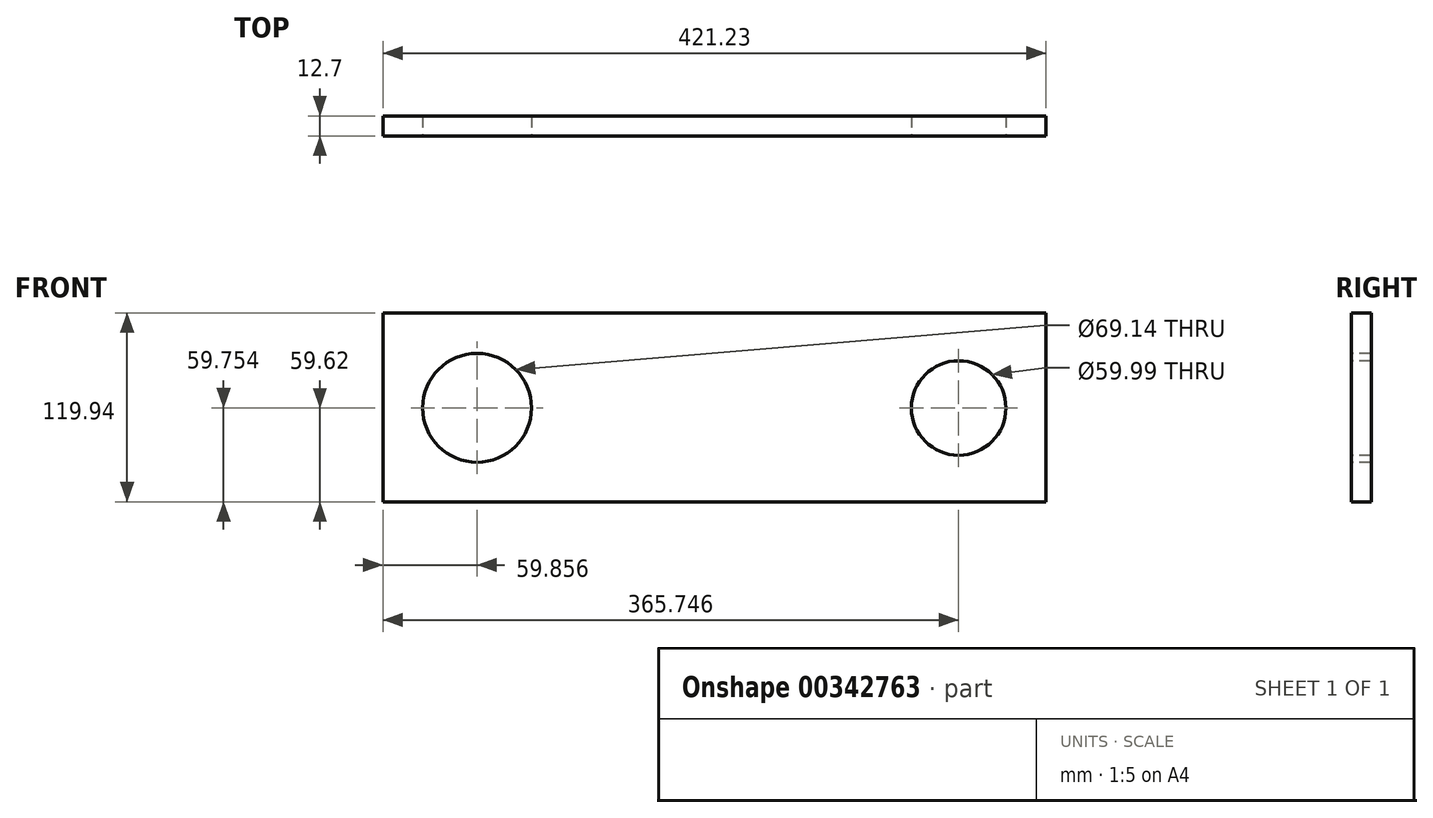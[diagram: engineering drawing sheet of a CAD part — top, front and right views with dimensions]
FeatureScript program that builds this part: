
annotation { "Feature Type Name" : "Feature", "Feature Type Description" : "" }
export const myFeature = defineFeature(function(context is Context, id is Id, definition is map)
    precondition{}
    {
        {
            var Q0;
            Q0=qCreatedBy(makeId("Front.planeOp"),FACE);
            var sketch = newSketch(context, id + "F0", { "sketchPlane" : qUnion([Q0])});
            skLineSegment(sketch, "E0.bottom", {"start": v(-215.15, 65.2) * mm, "end": v(206.08, 65.2) * mm});
            skLineSegment(sketch, "E0.top", {"start": v(-215.15, -54.73) * mm, "end": v(206.08, -54.73) * mm});
            skLineSegment(sketch, "E0.left", {"start": v(-215.15, 65.2) * mm, "end": v(-215.15, -54.73) * mm});
            skLineSegment(sketch, "E0.right", {"start": v(206.08, 65.2) * mm, "end": v(206.08, -54.73) * mm});
            skLineSegment(sketch, "E1.0", {"start": v(-215.15, 5.24) * mm, "end": v(206.08, 5.24) * mm, "construction": true});
            skLineSegment(sketch, "E2.0", {"start": v(-189.75, 65.2) * mm, "end": v(-189.75, -54.73) * mm, "construction": true});
            skLineSegment(sketch, "E3.0", {"start": v(180.68, 65.2) * mm, "end": v(180.68, -54.73) * mm, "construction": true});
            skLineSegment(sketch, "E4.0", {"start": v(-120.61, 65.2) * mm, "end": v(-120.61, -54.73) * mm, "construction": true});
            skLineSegment(sketch, "E5.0", {"start": v(120.69, 65.2) * mm, "end": v(120.69, -54.73) * mm, "construction": true});
            skCircle(sketch, "E6", {"center": v(-155.3, 5.02) * mm, "radius": 34.57 * mm});
            skCircle(sketch, "E7", {"center": v(150.6, 4.9) * mm, "radius": 30 * mm});
            skSolve(sketch);
        }
        {
            var Q0;
            Q0 = qSketchRegion(id + "F0", true);
            extrude(context, id + "F1", {"entities" : qUnion([Q0]), "oppositeDirection" : true, "depth" : 12.7 * mm});
        }
    });
